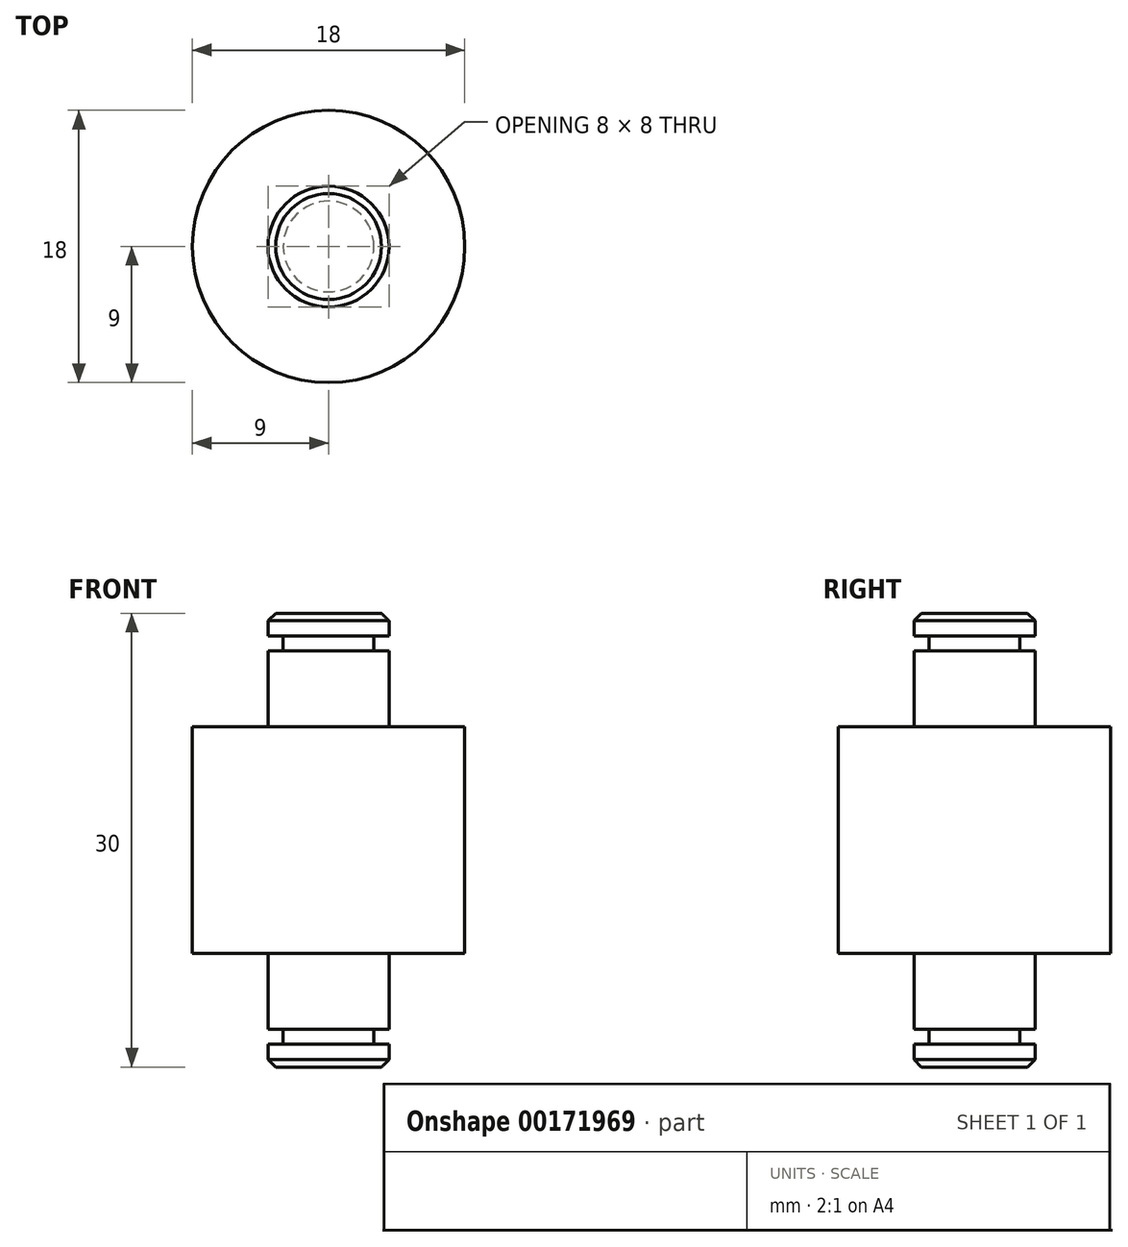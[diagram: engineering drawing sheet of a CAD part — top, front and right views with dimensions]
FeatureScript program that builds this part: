
annotation { "Feature Type Name" : "Feature", "Feature Type Description" : "" }
export const myFeature = defineFeature(function(context is Context, id is Id, definition is map)
    precondition{}
    {
        {
            var Q0;
            Q0=qCreatedBy(makeId("Top.planeOp"),FACE);
            var sketch = newSketch(context, id + "F0", { "sketchPlane" : qUnion([Q0])});
            skCircle(sketch, "E0", {"center": v(0, 0) * mm, "radius": 9 * mm});
            skSolve(sketch);
        }
        {
            var Q0;
            Q0=makeQuery(id+"F0.imprint","IMPRINT",FACE,{"disambiguationData":[TD([[makeQuery(id+"F0.imprint","IMPRINT",EDGE,{"derivedFrom":sQuery(id+"F0.wireOp",EDGE,"E0")}),1.0]])]});
            extrude(context, id + "F1", {"entities" : qUnion([Q0]), "endBound" : BoundingType.SYMMETRIC, "depth" : 15 * mm});
        }
        {
            var Q0;
            Q0=makeQuery(id+"F1.opExtrude","CAP_FACE",FACE,{"disambiguationData":[OSD([sQuery(id+"F0.wireOp",EDGE,"E0")])],"isStart":false});
            var sketch = newSketch(context, id + "F2", { "sketchPlane" : qUnion([Q0])});
            skCircle(sketch, "E1", {"center": v(0, 0) * mm, "radius": 4 * mm});
            skSolve(sketch);
        }
        {
            var Q0;
            Q0 = qSketchRegion(id + "F2", true);
            extrude(context, id + "F3", {"entities" : qUnion([Q0]), "operationType" : NewBodyOperationType.ADD, "depth" : 7.5 * mm});
        }
        {
            var Q0;
            Q0=makeQuery(id+"F3.opExtrude","CAP_EDGE",EDGE,{"disambiguationData":[OSD([sQuery(id+"F2.wireOp",EDGE,"E1")])],"isStart":false});
            chamfer(context, id + "F4", {"entities" : qUnion([Q0]), "chamferType" : ChamferType.OFFSET_ANGLE, "width" : .5 * mm, "oppositeDirection" : false, "angle" : 45 * degree, "tangentPropagation" : true});
        }
        {
            var Q0;
            Q0=qCreatedBy(makeId("Right.planeOp"),FACE);
            var sketch = newSketch(context, id + "F5", { "sketchPlane" : qUnion([Q0])});
            skLineSegment(sketch, "E2.bottom", {"start": v(4, 13.5) * mm, "end": v(3, 13.5) * mm});
            skLineSegment(sketch, "E2.top", {"start": v(4, 12.5) * mm, "end": v(3, 12.5) * mm});
            skLineSegment(sketch, "E2.left", {"start": v(4, 13.5) * mm, "end": v(4, 12.5) * mm});
            skLineSegment(sketch, "E2.right", {"start": v(3, 13.5) * mm, "end": v(3, 12.5) * mm});
            skSolve(sketch);
        }
        {
            var Q0;
            Q0 = qSketchRegion(id + "F5", true);
            var Q1;
            Q1=makeQuery(id+"F3.opExtrude","SWEPT_FACE",FACE,{"disambiguationData":[OSD([sQuery(id+"F2.wireOp",EDGE,"E1")])]});
            revolve(context, id + "F6", {"operationType" : NewBodyOperationType.REMOVE, "entities" : qUnion([Q0]), "axis" : qUnion([Q1]), "revolveType" : RevolveType.FULL, "oppositeDirection" : true});
        }
        {
            var Q0;
            Q0=makeQuery(id+"F3.opExtrude","CAP_FACE",FACE,{"disambiguationData":[OSD([sQuery(id+"F2.wireOp",EDGE,"E1")])],"isStart":false});
            var Q1;
            Q1=makeQuery(id+"F4.opChamfer","BLEND_FACE",FACE,{"disambiguationData":[OSD([sQuery(id+"F2.wireOp",EDGE,"E1")])]});
            var Q2;
            {var subQ0=sQuery(id+"F2.wireOp",EDGE,"E1");Q2=makeQuery(id+"F6.boolean.opBoolean","SPLIT",FACE,{"disambiguationData":[TD([makeQuery(id+"F4.opChamfer","BLEND_FACE",FACE,{"disambiguationData":[OSD([subQ0])]})])],"derivedFrom":makeQuery(id+"F3.opExtrude","SWEPT_FACE",FACE,{"disambiguationData":[OSD([subQ0])]})});}
            var Q3;
            Q3=makeQuery(id+"F6.boolean.opBoolean","SPLIT",FACE,{"disambiguationData":[TD([makeQuery(id+"F1.opExtrude","CAP_FACE",FACE,{"disambiguationData":[OSD([sQuery(id+"F0.wireOp",EDGE,"E0")])],"isStart":false})])],"derivedFrom":makeQuery(id+"F3.opExtrude","SWEPT_FACE",FACE,{"disambiguationData":[OSD([sQuery(id+"F2.wireOp",EDGE,"E1")])]})});
            var Q4;
            Q4=makeQuery(id+"F6.boolean.opBoolean","COPY",FACE,{"derivedFrom":makeQuery(id+"F6.opRevolve","SWEPT_FACE",FACE,{"disambiguationData":[OSD([sQuery(id+"F5.wireOp",EDGE,"E2.right")])]})});
            var Q5;
            Q5=makeQuery(id+"F6.boolean.opBoolean","COPY",FACE,{"derivedFrom":makeQuery(id+"F6.opRevolve","SWEPT_FACE",FACE,{"disambiguationData":[OSD([sQuery(id+"F5.wireOp",EDGE,"E2.top")])]})});
            var Q6;
            Q6=makeQuery(id+"F6.boolean.opBoolean","COPY",FACE,{"derivedFrom":makeQuery(id+"F6.opRevolve","SWEPT_FACE",FACE,{"disambiguationData":[OSD([sQuery(id+"F5.wireOp",EDGE,"E2.bottom")])]})});
            var Q7;
            Q7=qCreatedBy(makeId("Top.planeOp"),FACE);
            mirror(context, id + "F7", {"patternType" : MirrorType.FACE, "faces" : qUnion([Q0, Q1, Q2, Q3, Q4, Q5, Q6]), "mirrorPlane" : qUnion([Q7])});
        }
    });
